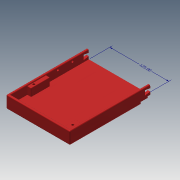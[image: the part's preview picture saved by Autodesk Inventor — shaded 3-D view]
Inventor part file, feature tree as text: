
AUTODESK INVENTOR PART (.ipt)
format: ipt  version: 2019 (Build 230136000, 136)  size: 279,040 bytes
history: native  units: mm
features: sketch x10, extrude x9, projected_geometry x3, other x2, fillet x2, plane x1
ambient origin geometry x8: Origin, YZ Plane, XZ Plane, XY Plane, X Axis, Y Axis, Z Axis, Center Point
bodies: Solid1 (feature_tree)
feature tree (27):
  other  "Annotations"
  extrude  "Extrusion1"  Depth=150.0mm
  extrude  "Extrusion2"  Depth=5.0mm
  extrude  "Extrusion3"  Depth=20.0mm TaperAngle=0.0deg
  extrude  "Extrusion4"  Depth=3.0mm
  fillet  "Fillet1"  Radius=20.0mm
  sketch  "Sketch11"  dims[d23=20.0mm d24=0.0mm d25=2.0mm]
  sketch  "Sketch12"  dims[d37=2.5mm d38=0.0mm d39=35.0mm d40=0.0mm]
  extrude  "Extrusion8"  Depth=2.0mm
  extrude  "Extrusion9"  Depth=35.0mm
  fillet  "Fillet4"  [1 undecoded]
  extrude  "Extrusion10"  Depth=40.0mm
  extrude  "Extrusion11"  TaperAngle=0.0deg  [1 undecoded]
  plane  "Work Plane3"
  extrude  "Extrusion13"  Depth=13.0mm
  sketch  "Sketch1"  dims[d0=135.0mm d1=150.0mm]
  sketch  "Sketch3"  dims[d2=8.0mm d3=0.0mm d4=5.0mm]
  projected_geometry  "Projected Loop2"
  sketch  "Sketch4"  dims[d5=5.0mm d6=20.0mm d7=0.0mm]
  projected_geometry  "Projected Loop3"
  sketch  "Sketch6"  dims[d8=3.0mm d9=3.0mm d10=20.0mm d11=0.0mm]
  sketch  "Sketch15"  dims[d41=8.0mm d42=40.0mm]
  projected_geometry  "Projected Loop7"
  sketch  "Sketch16"  dims[d43=0.0mm d44=0.0mm]
  sketch  "Sketch17"  dims[d45=40.0mm d46=13.0mm]
  sketch  "Sketch21"  dims[d47=16.0mm d48=0.0mm d49=1.0mm d50=4.5mm d51=3.5mm d52=9.0mm d53=4.5mm d54=6.0mm d56=12.0mm d57=0.0mm d60=4.5mm d61=4.5mm d62=30.8mm d64=5.0mm d65=0.0mm d66=0.0mm d67=100.0mm d76=-1.5mm d78=7.5mm d79=7.5mm d80=3.15mm d81=0.0mm d83=6.0mm d85=6.0mm d86=0.0mm d87=11.0mm d88=2.0mm d89=2.0mm d90=12.5mm d73=4.870635mm d74=1.41766mm d75=125.0mm]
  other  "Linear Dimension 1"
note: 2 required parameter values undecoded (feature->parameter linkage not recoverable at this tier; creation-order binding heuristic only, values carry confidence <= 0.55)
